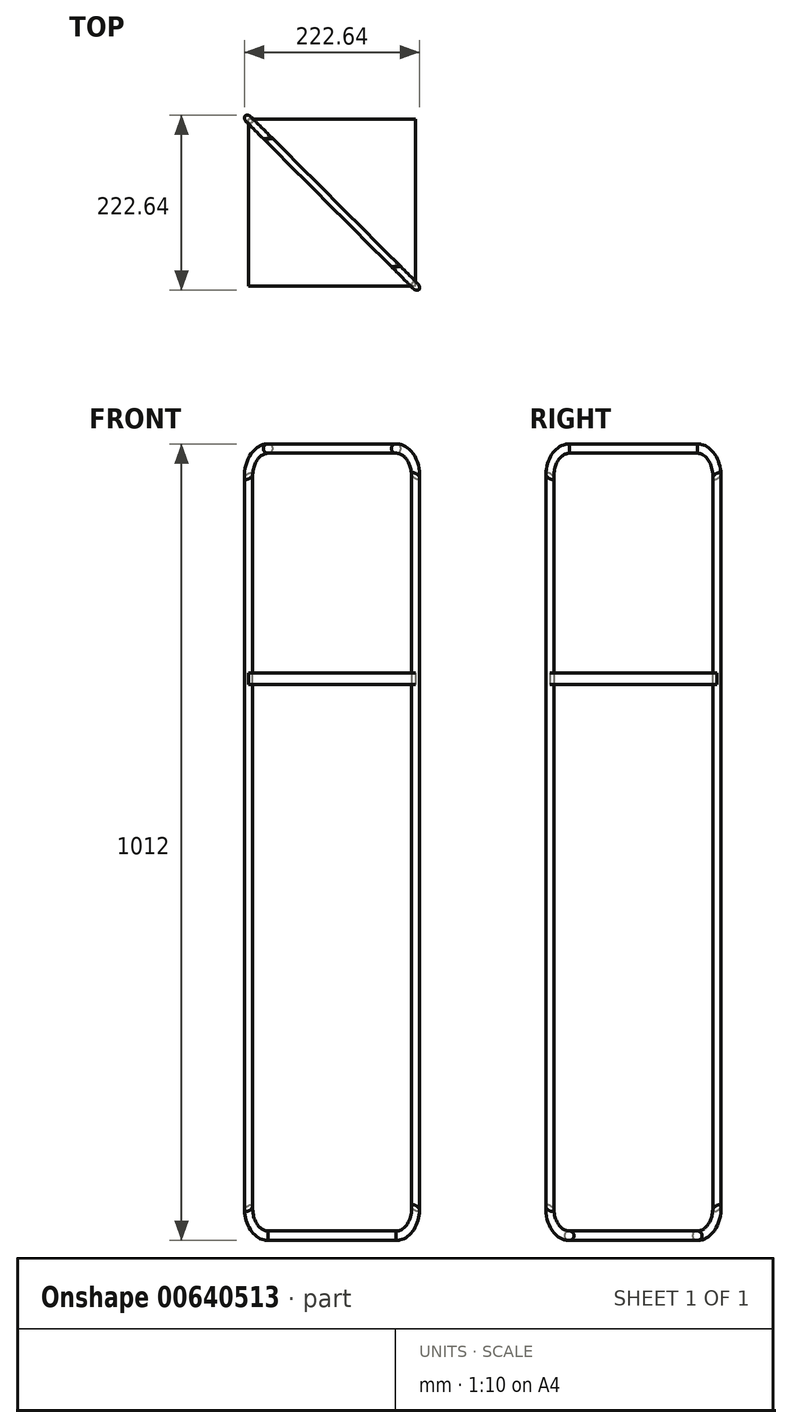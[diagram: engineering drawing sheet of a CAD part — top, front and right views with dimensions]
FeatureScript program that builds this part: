
annotation { "Feature Type Name" : "Feature", "Feature Type Description" : "" }
export const myFeature = defineFeature(function(context is Context, id is Id, definition is map)
    precondition{}
    {
        {
            var Q0;
            Q0=qCreatedBy(makeId("Front.planeOp"),FACE);
            var sketch = newSketch(context, id + "F0", { "sketchPlane" : qUnion([Q0])});
            skLineSegment(sketch, "E0", {"start": v(0, 0) * mm, "end": v(0, 1000) * mm, "construction": true});
            skSolve(sketch);
        }
        {
            var Q0;
            Q0=sQuery(id+"F0.wireOp",EDGE,"E0");
            cPlane(context, id + "F1", {"entities" : qUnion([Q0]), "cplaneType" : CPlaneType.LINE_ANGLE, "offset" : 25 * mm, "angle" : 45 * degree, "width" : 150 * mm, "height" : 150 * mm});
        }
        {
            var Q0;
            Q0=qCreatedBy(id+"F1.planeOp",FACE);
            var sketch = newSketch(context, id + "F2", { "sketchPlane" : qUnion([Q0])});
            skLineSegment(sketch, "E1.bottom", {"start": v(150, 0) * mm, "end": v(-150, 0) * mm, "construction": true});
            skLineSegment(sketch, "E1.top", {"start": v(150, 1000) * mm, "end": v(-150, 1000) * mm, "construction": true});
            skLineSegment(sketch, "E1.left", {"start": v(150, 0) * mm, "end": v(150, 1000) * mm, "construction": true});
            skLineSegment(sketch, "E1.right", {"start": v(-150, 0) * mm, "end": v(-150, 1000) * mm, "construction": true});
            skPoint(sketch, "E1.middle", {"position": v(0, 500) * mm});
            skLineSegment(sketch, "E2.bottom", {"start": v(-115, 1000) * mm, "end": v(115, 1000) * mm});
            skLineSegment(sketch, "E2.top", {"start": v(-115, 0) * mm, "end": v(115, 0) * mm});
            skLineSegment(sketch, "E2.left", {"start": v(-150, 965) * mm, "end": v(-150, 35) * mm});
            skLineSegment(sketch, "E2.right", {"start": v(150, 965) * mm, "end": v(150, 35) * mm});
            skPoint(sketch, "E3.visualSharp", {"position": v(-150, 1000) * mm});
            skArc(sketch, "E3.filletArc", {"start": v(-115, 1000) * mm, "mid": v(-139.75, 989.75) * mm, "end": v(-150, 965) * mm});
            skPoint(sketch, "E4.visualSharp", {"position": v(150, 1000) * mm});
            skArc(sketch, "E4.filletArc", {"start": v(150, 965) * mm, "mid": v(139.75, 989.75) * mm, "end": v(115, 1000) * mm});
            skPoint(sketch, "E5.visualSharp", {"position": v(150, 0) * mm});
            skArc(sketch, "E5.filletArc", {"start": v(115, 0) * mm, "mid": v(139.75, 10.25) * mm, "end": v(150, 35) * mm});
            skPoint(sketch, "E6.visualSharp", {"position": v(-150, 0) * mm});
            skArc(sketch, "E6.filletArc", {"start": v(-150, 35) * mm, "mid": v(-139.75, 10.25) * mm, "end": v(-115, 0) * mm});
            skLineSegment(sketch, "E7", {"start": v(0, 1000) * mm, "end": v(0, 700) * mm, "construction": true});
            skSolve(sketch);
        }
        {
            var Q0;
            Q0=qCreatedBy(makeId("Right.planeOp"),FACE);
            var sketch = newSketch(context, id + "F3", { "sketchPlane" : qUnion([Q0])});
            skCircle(sketch, "E8", {"center": v(0, 0) * mm, "radius": 6 * mm});
            skSolve(sketch);
        }
        {
            var Q0;
            Q0=qSketchRegion(id+"F3",true);
            var Q1;
            Q1=sQuery(id+"F2.wireOp",EDGE,"E6.filletArc");
            var Q2;
            Q2=sQuery(id+"F2.wireOp",EDGE,"E2.top");
            var Q3;
            Q3=sQuery(id+"F2.wireOp",EDGE,"E2.left");
            var Q4;
            Q4=sQuery(id+"F2.wireOp",EDGE,"E3.filletArc");
            var Q5;
            Q5=sQuery(id+"F2.wireOp",EDGE,"E2.bottom");
            var Q6;
            Q6=sQuery(id+"F2.wireOp",EDGE,"E4.filletArc");
            var Q7;
            Q7=sQuery(id+"F2.wireOp",EDGE,"E2.right");
            var Q8;
            Q8=sQuery(id+"F2.wireOp",EDGE,"E5.filletArc");
            sweep(context, id + "F4", {"profiles" : qUnion([Q0]), "path" : qUnion([Q1, Q2, Q3, Q4, Q5, Q6, Q7, Q8])});
        }
        {
            var Q0;
            Q0=sQuery(id+"F2.wireOp",VERTEX,"E7.end");
            var Q1;
            Q1=qCreatedBy(makeId("Top.planeOp"),FACE);
            cPlane(context, id + "F5", {"entities" : qUnion([Q0, Q1]), "cplaneType" : CPlaneType.PLANE_POINT, "offset" : 25 * mm, "width" : 150 * mm, "height" : 150 * mm});
        }
        {
            var Q0;
            Q0=qCreatedBy(id+"F5.planeOp",FACE);
            var sketch = newSketch(context, id + "F6", { "sketchPlane" : qUnion([Q0])});
            skLineSegment(sketch, "E9.bottom", {"start": v(106.07, -106.07) * mm, "end": v(-106.07, -106.07) * mm});
            skLineSegment(sketch, "E9.top", {"start": v(106.07, 106.07) * mm, "end": v(-106.07, 106.07) * mm});
            skLineSegment(sketch, "E9.left", {"start": v(106.07, -106.07) * mm, "end": v(106.07, 106.07) * mm});
            skLineSegment(sketch, "E9.right", {"start": v(-106.07, -106.07) * mm, "end": v(-106.07, 106.07) * mm});
            skPoint(sketch, "E9.middle", {"position": v(0, 0) * mm});
            skPoint(sketch, "E10", {"position": v(0, -106.07) * mm});
            skPoint(sketch, "E11", {"position": v(-106.07, 0) * mm});
            skSolve(sketch);
        }
        {
            var Q0;
            Q0 = qSketchRegion(id + "F6", true);
            extrude(context, id + "F7", {"entities" : qUnion([Q0]), "depth" : 15 * mm, "offsetDistance" : 25 * mm});
        }
    });
